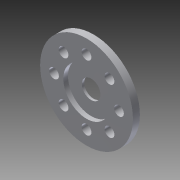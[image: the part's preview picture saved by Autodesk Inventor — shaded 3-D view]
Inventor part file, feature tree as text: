
AUTODESK INVENTOR PART (.ipt)
format: ipt  version: 2013 (Build 170138000, 138)  size: 113,152 bytes
history: native  units: mm
features: sketch x3, hole x2, extrude x1, pattern_circular x1
ambient origin geometry x8: Origin, YZ Plane, XZ Plane, XY Plane, X Axis, Y Axis, Z Axis, Center Point
feature tree (7):
  extrude  "押し出し2"  Depth=20.0mm
  hole  "穴2"  [1 undecoded]
  hole  "穴3"  [1 undecoded]
  pattern_circular  "円形状パターン2"  [2 undecoded]
  sketch  "スケッチ1"
  sketch  "スケッチ3"
  sketch  "スケッチ4"
note: 4 required parameter values undecoded (feature->parameter linkage not recoverable at this tier; creation-order binding heuristic only, values carry confidence <= 0.55)
